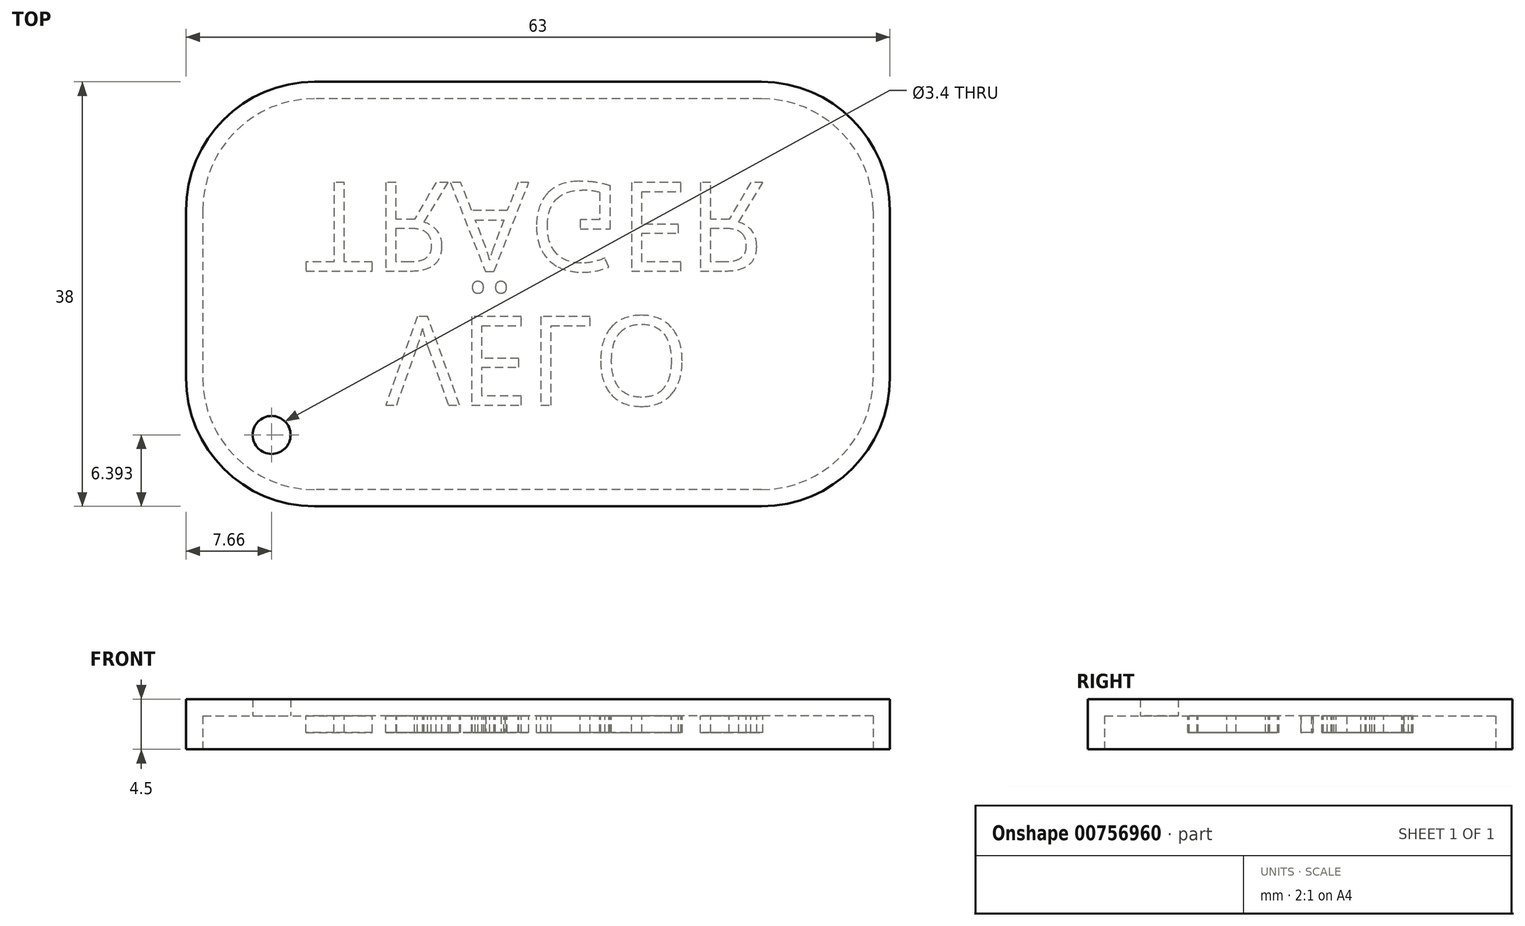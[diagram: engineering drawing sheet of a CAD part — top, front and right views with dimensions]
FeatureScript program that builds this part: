
annotation { "Feature Type Name" : "Feature", "Feature Type Description" : "" }
export const myFeature = defineFeature(function(context is Context, id is Id, definition is map)
    precondition{}
    {
        {
            var Q0;
            Q0=qCreatedBy(makeId("Top.planeOp"),FACE);
            var sketch = newSketch(context, id + "F0", { "sketchPlane" : qUnion([Q0])});
            skLineSegment(sketch, "E0.bottom", {"start": v(30, 17.5) * mm, "end": v(-30, 17.5) * mm});
            skLineSegment(sketch, "E0.top", {"start": v(30, -17.5) * mm, "end": v(-30, -17.5) * mm});
            skLineSegment(sketch, "E0.left", {"start": v(30, 17.5) * mm, "end": v(30, -17.5) * mm});
            skLineSegment(sketch, "E0.right", {"start": v(-30, 17.5) * mm, "end": v(-30, -17.5) * mm});
            skPoint(sketch, "E0.middle", {"position": v(0, 0) * mm});
            skSolve(sketch);
        }
        {
            var Q0;
            Q0=makeQuery(id+"F0.imprint","IMPRINT",FACE,{"disambiguationData":[TD([[makeQuery(id+"F0.imprint","IMPRINT",EDGE,{"derivedFrom":sQuery(id+"F0.wireOp",EDGE,"E0.bottom")}),1.0]])]});
            extrude(context, id + "F1", {"entities" : qUnion([Q0]), "depth" : 3 * mm, "offsetDistance" : 25 * mm});
        }
        {
            var Q0;
            Q0=makeQuery(id+"F1.opExtrude","SWEPT_EDGE",EDGE,{"disambiguationData":[OSD([sQuery(id+"F0.wireOp",EDGE,"E0.bottom"),sQuery(id+"F0.wireOp",EDGE,"E0.left")])]});
            var Q1;
            Q1=makeQuery(id+"F1.opExtrude","SWEPT_EDGE",EDGE,{"disambiguationData":[OSD([sQuery(id+"F0.wireOp",EDGE,"E0.top"),sQuery(id+"F0.wireOp",EDGE,"E0.right")])]});
            var Q2;
            Q2=makeQuery(id+"F1.opExtrude","SWEPT_EDGE",EDGE,{"disambiguationData":[OSD([sQuery(id+"F0.wireOp",EDGE,"E0.top"),sQuery(id+"F0.wireOp",EDGE,"E0.left")])]});
            var Q3;
            Q3=makeQuery(id+"F1.opExtrude","SWEPT_EDGE",EDGE,{"disambiguationData":[OSD([sQuery(id+"F0.wireOp",EDGE,"E0.bottom"),sQuery(id+"F0.wireOp",EDGE,"E0.right")])]});
            fillet(context, id + "F2", {"entities" : qUnion([Q0, Q1, Q2, Q3]), "radius" : 10 * mm, "tangentPropagation" : true, "allowEdgeOverflow" : false});
        }
        {
            var Q0;
            Q0=makeQuery(id+"F1.opExtrude","CAP_FACE",FACE,{"disambiguationData":[OSD([sQuery(id+"F0.wireOp",EDGE,"E0.bottom"),sQuery(id+"F0.wireOp",EDGE,"E0.top"),sQuery(id+"F0.wireOp",EDGE,"E0.left"),sQuery(id+"F0.wireOp",EDGE,"E0.right")])],"isStart":true});
            shell(context, id + "F3", {"entities" : qUnion([Q0]), "thickness" : 1.5 * mm, "oppositeDirection" : true});
        }
        {
            var Q0;
            Q0=makeQuery(id+"F3.opShell","OFFSET_FACE",FACE,{"disambiguationData":[OSD([sQuery(id+"F0.wireOp",EDGE,"E0.bottom"),sQuery(id+"F0.wireOp",EDGE,"E0.top"),sQuery(id+"F0.wireOp",EDGE,"E0.left"),sQuery(id+"F0.wireOp",EDGE,"E0.right")])]});
            var sketch = newSketch(context, id + "F4", { "sketchPlane" : qUnion([Q0])});
            skText(sketch, "E1", { "text": "VELO", "fontName": "OpenSans-Regular.ttf"});
            skText(sketch, "E2", { "text": "TRÄGER", "fontName": "OpenSans-Regular.ttf"});
            const initialGuessF4  = {"E1": [-0.01363, 0.002, 1, 0, 0.008], "E2": [-0.02086, -0.01, 1, 0, 0.008]};
            skSetInitialGuess(sketch, initialGuessF4);
            skSolve(sketch);
        }
        {
            var Q0;
            Q0=qSketchRegion(id+"F4",true);
            extrude(context, id + "F5", {"entities" : qUnion([Q0]), "operationType" : NewBodyOperationType.ADD, "depth" : 1.5 * mm, "offsetDistance" : 25 * mm});
        }
        {
            var Q0;
            {var subQ0=sQuery(id+"F0.wireOp",EDGE,"E0.right");var subQ1=sQuery(id+"F0.wireOp",EDGE,"E0.top");var subQ2=sQuery(id+"F0.wireOp",EDGE,"E0.left");var subQ3=sQuery(id+"F0.wireOp",EDGE,"E0.bottom");Q0=makeQuery(id+"F5.boolean.opBoolean","SPLIT",FACE,{"disambiguationData":[TD([makeQuery(id+"F3.opShell","OFFSET_FACE",FACE,{"disambiguationData":[OSD([subQ3])]})])],"derivedFrom":makeQuery(id+"F3.opShell","OFFSET_FACE",FACE,{"disambiguationData":[OSD([subQ3,subQ1,subQ2,subQ0])]})});}
            var sketch = newSketch(context, id + "F6", { "sketchPlane" : qUnion([Q0])});
            skPoint(sketch, "E3", {"position": v(-23.84, 12.6) * mm});
            skSolve(sketch);
        }
        {
            var Q0;
            Q0=sQuery(id+"F6.wireOp",VERTEX,"E3");
            var Q1;
            Q1=makeQuery(id+"F1.opExtrude","SWEPT_BODY",BODY,{"disambiguationData":[OSD([sQuery(id+"F0.wireOp",EDGE,"E0.bottom"),sQuery(id+"F0.wireOp",EDGE,"E0.top"),sQuery(id+"F0.wireOp",EDGE,"E0.left"),sQuery(id+"F0.wireOp",EDGE,"E0.right")])]});
            hole(context, id + "F7", {"style" : HoleStyle.SIMPLE, "endStyle" : HoleEndStyle.THROUGH, "holeDiameter" : 3.4 * mm, "majorDiameter" : 5 * mm, "isTappedThrough" : true, "tappedDepth" : 12 * mm, "tapClearance" : 3, "locations" : qUnion([Q0]), "scope" : qUnion([Q1])});
        }
    });
